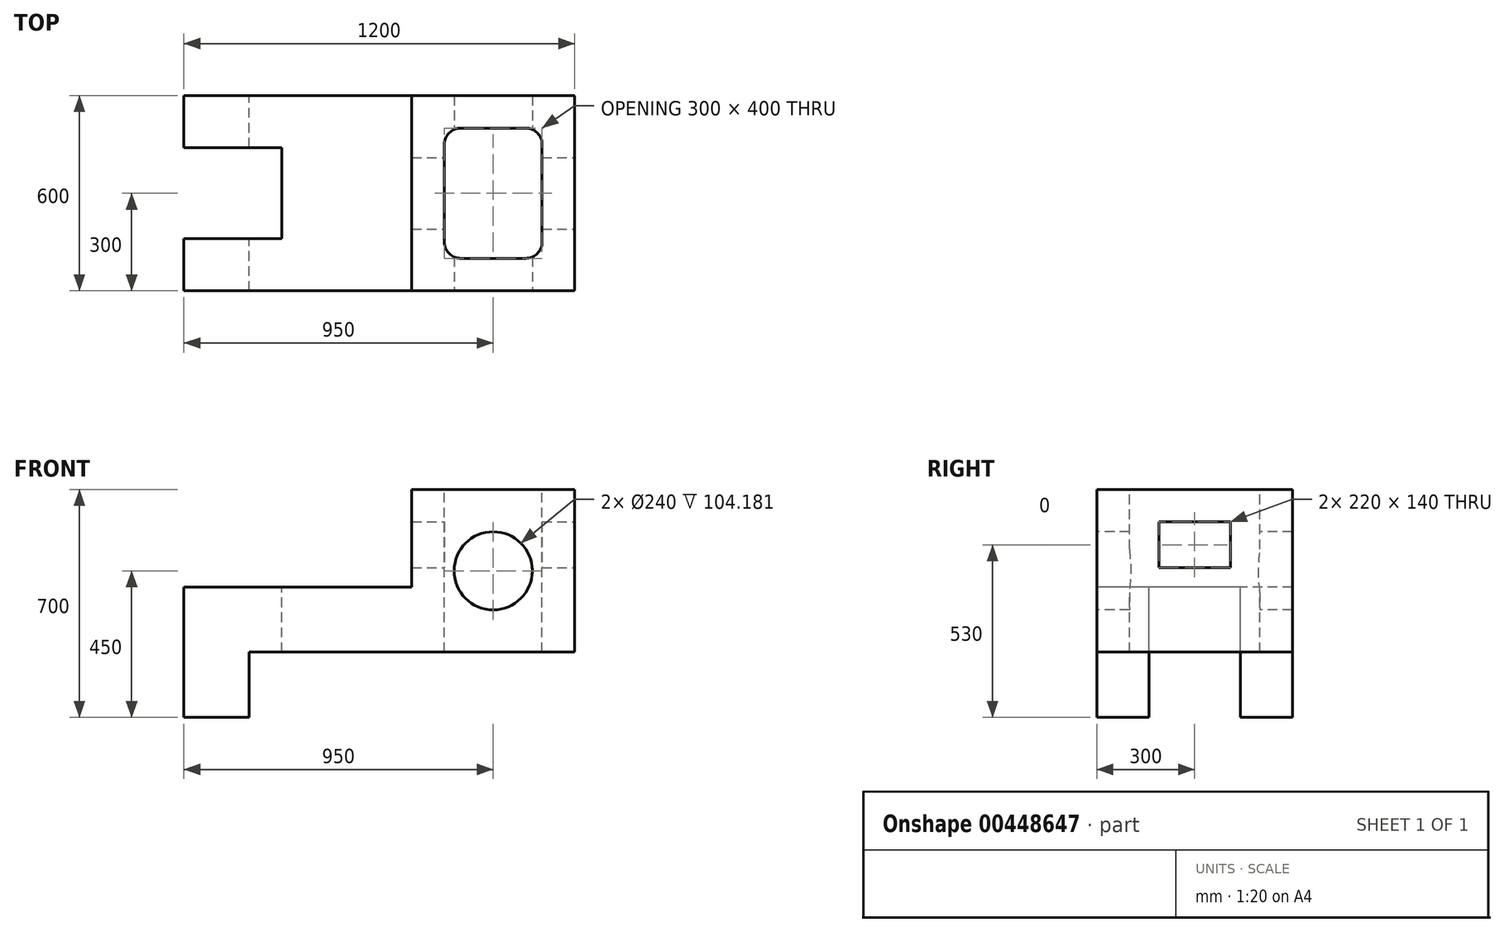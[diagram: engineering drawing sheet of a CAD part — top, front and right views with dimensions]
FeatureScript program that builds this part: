
annotation { "Feature Type Name" : "Feature", "Feature Type Description" : "" }
export const myFeature = defineFeature(function(context is Context, id is Id, definition is map)
    precondition{}
    {
        {
            var Q0;
            Q0=qCreatedBy(makeId("Top.planeOp"),FACE);
            var sketch = newSketch(context, id + "F0", { "sketchPlane" : qUnion([Q0])});
            skLineSegment(sketch, "E0.bottom", {"start": v(600, 300) * mm, "end": v(-600, 300) * mm});
            skLineSegment(sketch, "E0.top", {"start": v(600, -300) * mm, "end": v(-600, -300) * mm});
            skLineSegment(sketch, "E0.left", {"start": v(600, 300) * mm, "end": v(600, -300) * mm});
            skLineSegment(sketch, "E0.right", {"start": v(-600, 300) * mm, "end": v(-600, -300) * mm});
            skPoint(sketch, "E0.middle", {"position": v(0, 0) * mm});
            skSolve(sketch);
        }
        {
            var Q0;
            Q0=makeQuery(id+"F0.imprint","IMPRINT",FACE,{"disambiguationData":[TD([[makeQuery(id+"F0.imprint","IMPRINT",EDGE,{"derivedFrom":sQuery(id+"F0.wireOp",EDGE,"E0.bottom")}),1.0]])]});
            extrude(context, id + "F1", {"entities" : qUnion([Q0]), "depth" : 700 * mm});
        }
        {
            var Q0;
            Q0=makeQuery(id+"F1.opExtrude","CAP_FACE",FACE,{"disambiguationData":[OSD([sQuery(id+"F0.wireOp",EDGE,"E0.bottom"),sQuery(id+"F0.wireOp",EDGE,"E0.top"),sQuery(id+"F0.wireOp",EDGE,"E0.left"),sQuery(id+"F0.wireOp",EDGE,"E0.right")])],"isStart":false});
            var sketch = newSketch(context, id + "F2", { "sketchPlane" : qUnion([Q0])});
            skLineSegment(sketch, "E1", {"start": v(100, 300) * mm, "end": v(100, -300) * mm});
            skSolve(sketch);
        }
        {
            var Q0;
            Q0 = qSketchRegion(id + "F2", true);
            var Q1;
            {var subQ0=sQuery(id+"F2.wireOp",EDGE,"E1");Q1=makeQuery(id+"F2.imprint","IMPRINT",FACE,{"disambiguationData":[TD([[makeQuery(id+"F2.imprint","IMPRINT",EDGE,{"derivedFrom":subQ0}),-1.0]])]});}
            extrude(context, id + "F3", {"entities" : qUnion([Q0, Q1]), "operationType" : NewBodyOperationType.REMOVE, "oppositeDirection" : true, "depth" : 300 * mm});
        }
        {
            var Q0;
            Q0=makeQuery(id+"F1.opExtrude","CAP_FACE",FACE,{"disambiguationData":[OSD([sQuery(id+"F0.wireOp",EDGE,"E0.bottom"),sQuery(id+"F0.wireOp",EDGE,"E0.top"),sQuery(id+"F0.wireOp",EDGE,"E0.left"),sQuery(id+"F0.wireOp",EDGE,"E0.right")])],"isStart":true});
            var sketch = newSketch(context, id + "F4", { "sketchPlane" : qUnion([Q0])});
            skLineSegment(sketch, "E2", {"start": v(-400, 300) * mm, "end": v(-400, -300) * mm});
            skSolve(sketch);
        }
        {
            var Q0;
            Q0 = qSketchRegion(id + "F4", true);
            var Q1;
            {var subQ0=sQuery(id+"F4.wireOp",EDGE,"E2");Q1=makeQuery(id+"F4.imprint","IMPRINT",FACE,{"disambiguationData":[TD([[makeQuery(id+"F4.imprint","IMPRINT",EDGE,{"derivedFrom":subQ0}),1.0]])]});}
            extrude(context, id + "F5", {"entities" : qUnion([Q0, Q1]), "operationType" : NewBodyOperationType.REMOVE, "oppositeDirection" : true, "depth" : 200 * mm});
        }
        {
            var Q0;
            Q0=makeQuery(id+"F3.boolean.opBoolean","COPY",FACE,{"derivedFrom":makeQuery(id+"F3.opExtrude","CAP_FACE",FACE,{"disambiguationData":[OSD([sQuery(id+"F0.wireOp",EDGE,"E0.bottom"),sQuery(id+"F0.wireOp",EDGE,"E0.top"),sQuery(id+"F0.wireOp",EDGE,"E0.right"),sQuery(id+"F2.wireOp",EDGE,"E1")])],"isStart":false})});
            var sketch = newSketch(context, id + "F6", { "sketchPlane" : qUnion([Q0])});
            skLineSegment(sketch, "E3.bottom", {"start": v(-300, 140) * mm, "end": v(-900, 140) * mm});
            skLineSegment(sketch, "E3.top", {"start": v(-300, -140) * mm, "end": v(-900, -140) * mm});
            skLineSegment(sketch, "E3.left", {"start": v(-300, 140) * mm, "end": v(-300, -140) * mm});
            skLineSegment(sketch, "E3.right", {"start": v(-900, 140) * mm, "end": v(-900, -140) * mm});
            skPoint(sketch, "E3.middle", {"position": v(-600, 0) * mm});
            skSolve(sketch);
        }
        {
            var Q0;
            Q0 = qSketchRegion(id + "F6", true);
            extrude(context, id + "F7", {"entities" : qUnion([Q0]), "operationType" : NewBodyOperationType.REMOVE, "endBound" : BoundingType.THROUGH_ALL, "oppositeDirection" : true, "depth" : 25 * mm});
        }
        {
            var Q0;
            Q0=makeQuery(id+"F1.opExtrude","CAP_FACE",FACE,{"disambiguationData":[OSD([sQuery(id+"F0.wireOp",EDGE,"E0.bottom"),sQuery(id+"F0.wireOp",EDGE,"E0.top"),sQuery(id+"F0.wireOp",EDGE,"E0.left"),sQuery(id+"F0.wireOp",EDGE,"E0.right")])],"isStart":false});
            var sketch = newSketch(context, id + "F8", { "sketchPlane" : qUnion([Q0])});
            skLineSegment(sketch, "E4.bottom", {"start": v(450, 200) * mm, "end": v(250, 200) * mm});
            skLineSegment(sketch, "E4.top", {"start": v(450, -200) * mm, "end": v(250, -200) * mm});
            skLineSegment(sketch, "E4.left", {"start": v(500, 150) * mm, "end": v(500, -150) * mm});
            skLineSegment(sketch, "E4.right", {"start": v(200, 150) * mm, "end": v(200, -150) * mm});
            skPoint(sketch, "E4.middle", {"position": v(350, 0) * mm});
            skPoint(sketch, "E5.visualSharp", {"position": v(200, 200) * mm});
            skArc(sketch, "E5.filletArc", {"start": v(250, 200) * mm, "mid": v(214.64, 185.36) * mm, "end": v(200, 150) * mm});
            skPoint(sketch, "E6.visualSharp", {"position": v(500, 200) * mm});
            skArc(sketch, "E6.filletArc", {"start": v(500, 150) * mm, "mid": v(485.36, 185.36) * mm, "end": v(450, 200) * mm});
            skPoint(sketch, "E7.visualSharp", {"position": v(200, -200) * mm});
            skArc(sketch, "E7.filletArc", {"start": v(200, -150) * mm, "mid": v(214.64, -185.36) * mm, "end": v(250, -200) * mm});
            skPoint(sketch, "E8.visualSharp", {"position": v(500, -200) * mm});
            skArc(sketch, "E8.filletArc", {"start": v(450, -200) * mm, "mid": v(485.36, -185.36) * mm, "end": v(500, -150) * mm});
            skSolve(sketch);
        }
        {
            var Q0;
            Q0 = qSketchRegion(id + "F8", true);
            extrude(context, id + "F9", {"entities" : qUnion([Q0]), "operationType" : NewBodyOperationType.REMOVE, "endBound" : BoundingType.THROUGH_ALL, "oppositeDirection" : true, "depth" : 25 * mm});
        }
        {
            var Q0;
            Q0=makeQuery(id+"F1.opExtrude","SWEPT_FACE",FACE,{"disambiguationData":[OSD([sQuery(id+"F0.wireOp",EDGE,"E0.left")])]});
            var sketch = newSketch(context, id + "F10", { "sketchPlane" : qUnion([Q0])});
            skLineSegment(sketch, "E9.bottom", {"start": v(-110, 460) * mm, "end": v(110, 460) * mm});
            skLineSegment(sketch, "E9.top", {"start": v(-110, 600) * mm, "end": v(110, 600) * mm});
            skLineSegment(sketch, "E9.left", {"start": v(-110, 460) * mm, "end": v(-110, 600) * mm});
            skLineSegment(sketch, "E9.right", {"start": v(110, 460) * mm, "end": v(110, 600) * mm});
            skPoint(sketch, "E9.middle", {"position": v(0, 530) * mm});
            skPoint(sketch, "E9.middle.positionSnap0", {"position": v(0, 700) * mm});
            skPoint(sketch, "E9.centerSnap0", {"position": v(0, 700) * mm});
            skSolve(sketch);
        }
        {
            var Q0;
            Q0 = qSketchRegion(id + "F10", true);
            extrude(context, id + "F11", {"entities" : qUnion([Q0]), "operationType" : NewBodyOperationType.REMOVE, "endBound" : BoundingType.THROUGH_ALL, "oppositeDirection" : true, "depth" : 25 * mm});
        }
        {
            var Q0;
            Q0=makeQuery(id+"F1.opExtrude","SWEPT_FACE",FACE,{"disambiguationData":[OSD([sQuery(id+"F0.wireOp",EDGE,"E0.top")])]});
            var sketch = newSketch(context, id + "F12", { "sketchPlane" : qUnion([Q0])});
            skCircle(sketch, "E10", {"center": v(350, 450) * mm, "radius": 120 * mm});
            skSolve(sketch);
        }
        {
            var Q0;
            Q0 = qSketchRegion(id + "F12", true);
            extrude(context, id + "F13", {"entities" : qUnion([Q0]), "operationType" : NewBodyOperationType.REMOVE, "endBound" : BoundingType.THROUGH_ALL, "oppositeDirection" : true, "depth" : 25 * mm});
        }
    });
